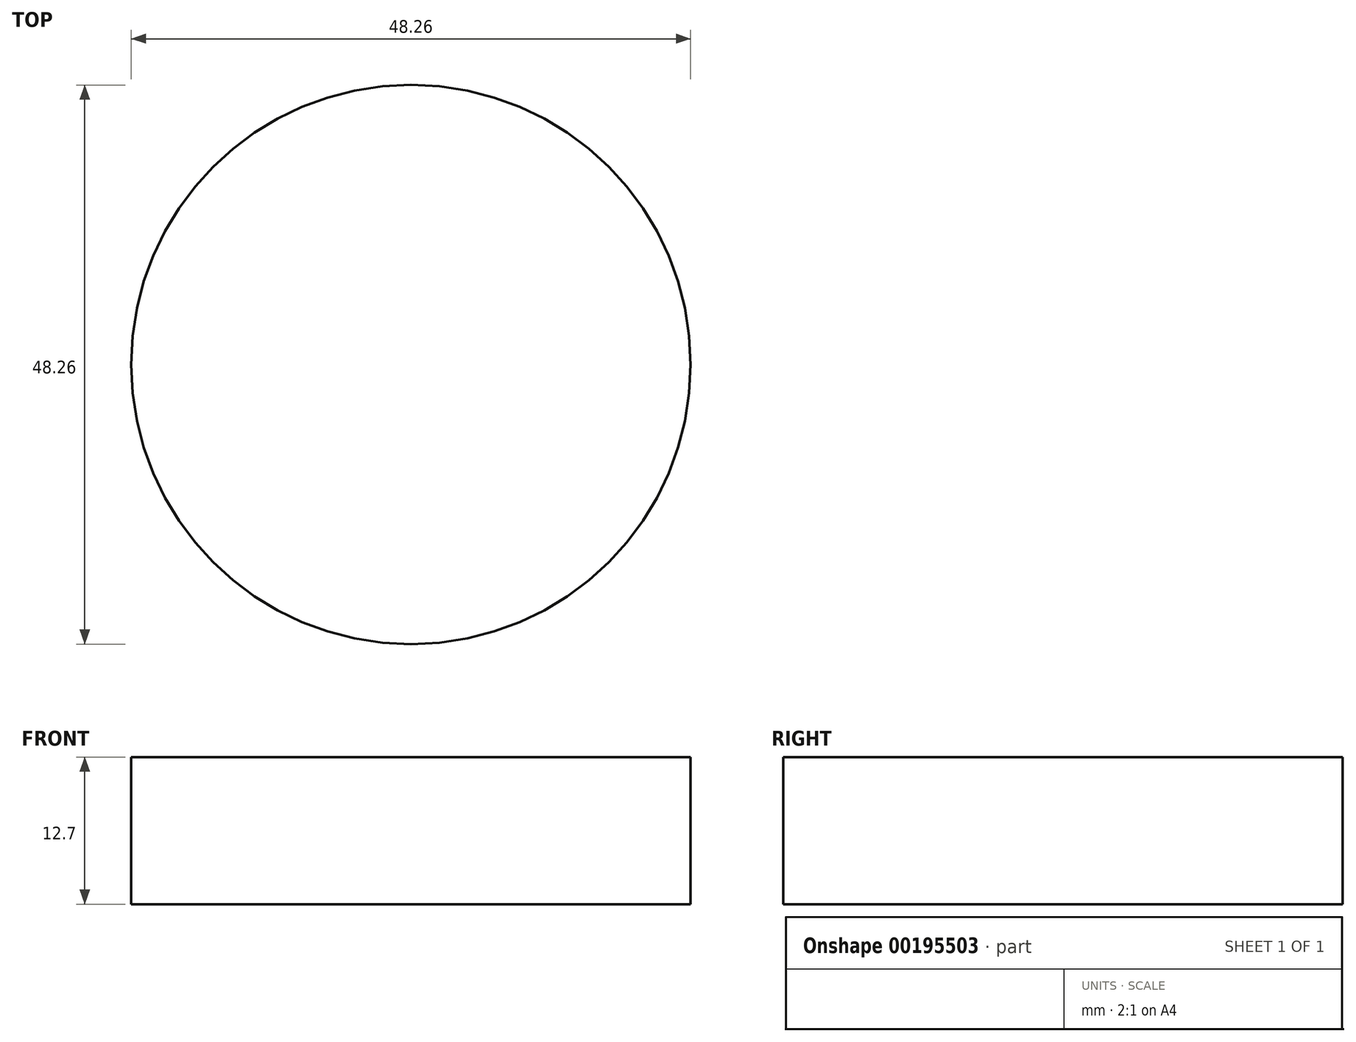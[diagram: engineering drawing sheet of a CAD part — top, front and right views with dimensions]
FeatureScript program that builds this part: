
annotation { "Feature Type Name" : "Feature", "Feature Type Description" : "" }
export const myFeature = defineFeature(function(context is Context, id is Id, definition is map)
    precondition{}
    {
        {
            var Q0;
            Q0=qCreatedBy(makeId("Top.planeOp"),FACE);
            var sketch = newSketch(context, id + "F0", { "sketchPlane" : qUnion([Q0])});
            skCircle(sketch, "E0", {"center": v(-56.58, 7.97) * mm, "radius": 24.13 * mm});
            skCircle(sketch, "E1", {"center": v(-56.58, 7.97) * mm, "radius": 12.77 * mm});
            skSolve(sketch);
        }
        {
            var Q0;
            Q0=makeQuery(id+"F0.imprint","IMPRINT",FACE,{"disambiguationData":[TD([[makeQuery(id+"F0.imprint","IMPRINT",EDGE,{"derivedFrom":sQuery(id+"F0.wireOp",EDGE,"E1")}),1.0]])]});
            var Q1;
            Q1=makeQuery(id+"F0.imprint","IMPRINT",FACE,{"disambiguationData":[TD([[makeQuery(id+"F0.imprint","IMPRINT",EDGE,{"derivedFrom":sQuery(id+"F0.wireOp",EDGE,"E0")}),1.0]])]});
            extrude(context, id + "F1", {"entities" : qUnion([Q0, Q1]), "depth" : 12.7 * mm});
        }
    });
